# Revit family: Ultra Outswing Door Sidelite
name_source: partatom
category: Doors
revit_build: Autodesk Revit 2017 (Build: 20160225_1515(x64)
units: mm (PartAtom-declared; Revit-internal decimal feet)

## family parameters
Always vertical = Yes
Cut with Voids When Loaded = No
Host = Wall
OmniClass Number = 23.30.10.00
OmniClass Title = Doors
Room Calculation Point = No
Shared = No

## types (1)
- Not a Type - Load Type Catalog
    1 Panel = No
    3 Inch Stile = Yes
    6 Inch Stile = No
    Acoustic Performance Data URL = http://www.kolbe-kolbe.com
    Air Water Structural Impact URL = http://www.kolbe-kolbe.com
    Description = Ultra Series Sidelite Entrace Door
    Divided Lites = No
    Energy Data and Tax Credits = http://www.kolbe-kolbe.com
    Ext Finish = Aluminum - Kolbe and Kolbe - Slate
    Full Lite = Yes
    Function = Interior
    Glazing Finish = Glass - Kolbe and Kolbe - Transparent
    Height = 6' - 10"
    Installation Services URL = http://www.kolbe-kolbe.com
    Int Finish = Wood - Kolbe and Kolbe - Pine
    Manufacturer = Kolbe & Kolbe Millwork Co., Inc.
    Model = UXD2068
    Optional Rail = Yes
    Panel Height = 6' - 9 1/8"
    Panel Width = 1' - 2 1/4"
    Product Documentation Link = http://www.kolbe-kolbe.com
    Product Name = Ultra Series Entrance Door
    Product Page URL = http://www.kolbe-kolbe.com
    ROLeft = 0' - 0"
    RORight = 0' - 0"
    ROTop = 0' - 0"
    Rough Height = 6' - 10 15/32"
    Rough Opening Left = No
    Rough Opening Right = No
    Rough Opening Top = No
    Rough Width = 1' - 4 1/2"
    Show Hinge and Swing = No
    Sill Finish = Aluminum - Kolbe and Kolbe - Bronze Anodized - Sill Finish
    Sill Height = 0' - 0 7/8"
    Standard Bottom Rail = No
    Standard Cross Rail = No
    URL = http://www.kolbe-kolbe.com
    Vertical Mullions = 2
    Wall Closure = By host
    Warranty = http://www.kolbe-kolbe.com
    Wide Bottom Rail = Yes
    Wide Cross Rail = Yes
    Width = 1' - 4"

## geometry (parser evidence)
native form markers: Blend x17, Sweep x16
no freeform markers — native parametric forms only
